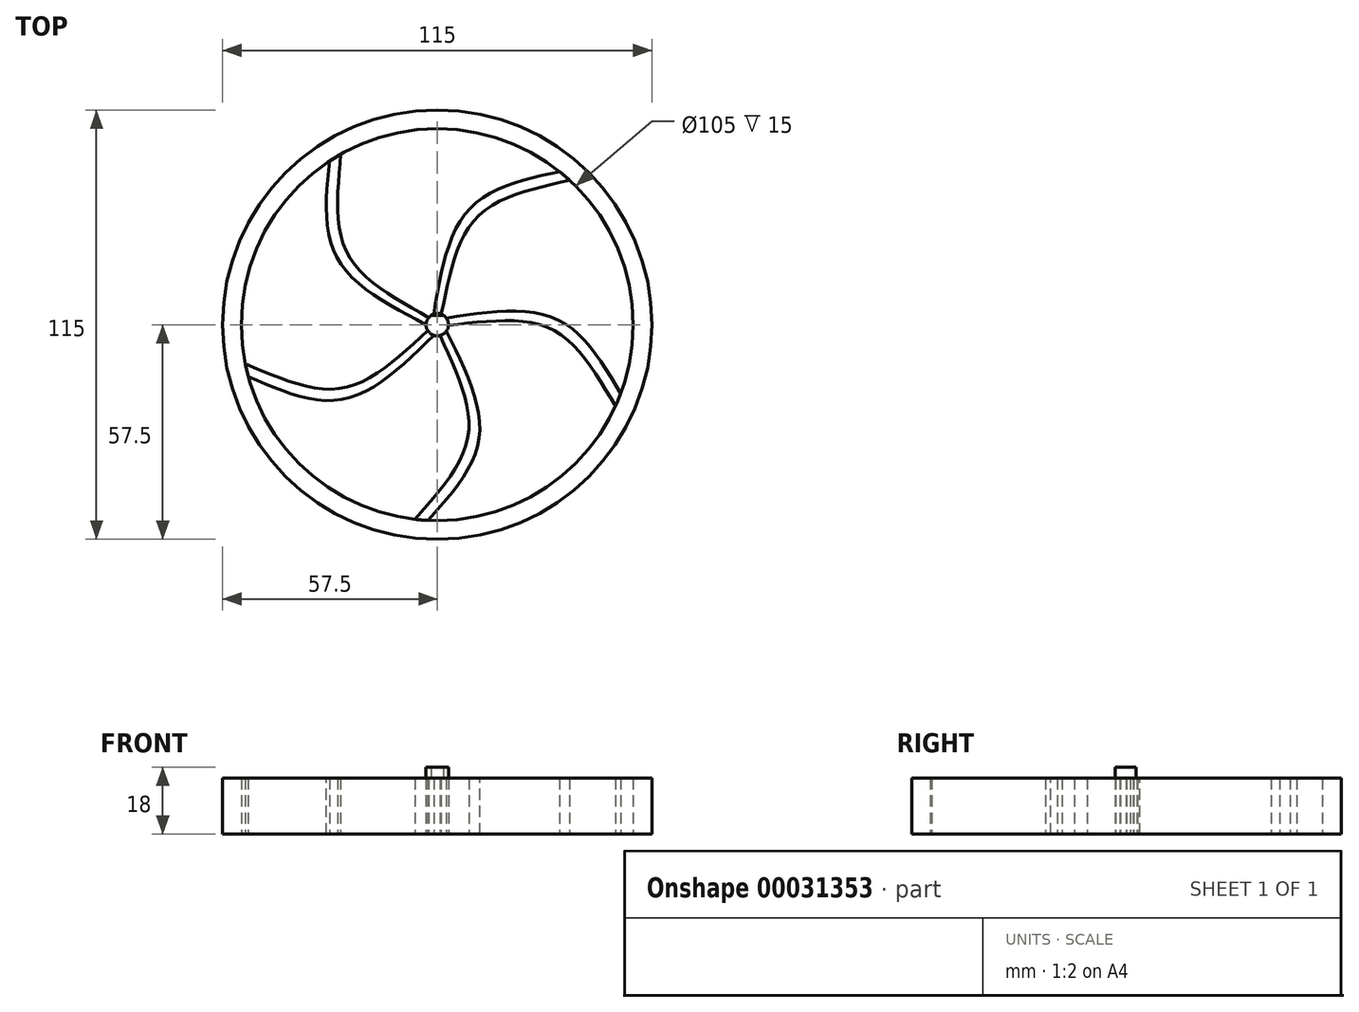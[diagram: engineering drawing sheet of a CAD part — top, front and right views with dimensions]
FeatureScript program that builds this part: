
annotation { "Feature Type Name" : "Feature", "Feature Type Description" : "" }
export const myFeature = defineFeature(function(context is Context, id is Id, definition is map)
    precondition{}
    {
        {
            var Q0;
            Q0=qCreatedBy(makeId("Top.planeOp"),FACE);
            var sketch = newSketch(context, id + "F0", { "sketchPlane" : qUnion([Q0])});
            skCircle(sketch, "E0", {"center": v(0, 0) * mm, "radius": 57.5 * mm});
            skCircle(sketch, "E1", {"center": v(0, 0) * mm, "radius": 52.5 * mm});
            skCircle(sketch, "E2", {"center": v(0, 0) * mm, "radius": 3 * mm});
            skFitSpline(sketch, "E3", {"points": [v(-3, 0) * mm, v(-26.82, 17.82) * mm, v(-28.86, 43.85) * mm], "startDerivative": vector(-56.96, 29.54) * mm, "endDerivative": vector(5.97, 58.41) * mm});
            skFitSpline(sketch, "E4", {"points": [v(-2.33, 1.89) * mm, v(-24.03, 18.91) * mm, v(-25.88, 45.68) * mm], "startDerivative": vector(-51.3, 30.03) * mm, "endDerivative": vector(4.5, 58.1) * mm});
            skSolve(sketch);
        }
        {
            var Q0;
            Q0 = qSketchRegion(id + "F0", true);
            var Q1;
            Q1=makeQuery(id+"F0.imprint","IMPRINT",FACE,{"disambiguationData":[TD([[makeQuery(id+"F0.imprint","IMPRINT",EDGE,{"derivedFrom":sQuery(id+"F0.wireOp",EDGE,"E2")}),1.0]])]});
            extrude(context, id + "F1", {"entities" : qUnion([Q0, Q1]), "depth" : 15 * mm});
        }
        {
            var Q0;
            {var subQ1=sQuery(id+"F0.wireOp",EDGE,"E3");Q0=makeQuery(id+"F0.imprint","IMPRINT",FACE,{"disambiguationData":[TD([[makeQuery(id+"F0.imprint","IMPRINT",EDGE,{"derivedFrom":subQ1}),-1.0]])]});}
            extrude(context, id + "F2", {"entities" : qUnion([Q0]), "depth" : 15 * mm});
        }
        {
            var Q0;
            Q0=qCreatedBy(makeId("Right.planeOp"),FACE);
            var sketch = newSketch(context, id + "F3", { "sketchPlane" : qUnion([Q0])});
            skLineSegment(sketch, "E5", {"start": v(0, 61.22) * mm, "end": v(0, -50.07) * mm});
            skSolve(sketch);
        }
        {
            var Q0;
            Q0=makeQuery(id+"F2.opExtrude","SWEPT_BODY",BODY,{"disambiguationData":[OSD([sQuery(id+"F0.wireOp",EDGE,"E1"),sQuery(id+"F0.wireOp",EDGE,"E2"),sQuery(id+"F0.wireOp",EDGE,"E3"),sQuery(id+"F0.wireOp",EDGE,"E4")])]});
            var Q1;
            Q1=sQuery(id+"F3.wireOp",EDGE,"E5");
            circularPattern(context, id + "F4", {"entities" : qUnion([Q0]), "axis" : qUnion([Q1]), "angle" : 360 * degree, "instanceCount" : 5, "equalSpace" : true});
        }
        {
            var Q0;
            Q0=makeQuery(id+"F1.opExtrude","CAP_FACE",FACE,{"disambiguationData":[OSD([sQuery(id+"F0.wireOp",EDGE,"E2")])],"isStart":false});
            var sketch = newSketch(context, id + "F5", { "sketchPlane" : qUnion([Q0])});
            skArc(sketch, "E6", {"start": v(-1.66, 2.5) * mm, "mid": v(0, -3) * mm, "end": v(1.66, 2.5) * mm});
            skLineSegment(sketch, "E7", {"start": v(-1.66, 2.5) * mm, "end": v(1.66, 2.5) * mm});
            skSolve(sketch);
        }
        {
            var Q0;
            Q0=makeQuery(id+"F5.imprint","IMPRINT",FACE,{"disambiguationData":[TD([[makeQuery(id+"F5.imprint","IMPRINT",EDGE,{"derivedFrom":sQuery(id+"F5.wireOp",EDGE,"E6")}),1.0]])]});
            extrude(context, id + "F6", {"entities" : qUnion([Q0]), "operationType" : NewBodyOperationType.ADD, "depth" : 3 * mm});
        }
    });
